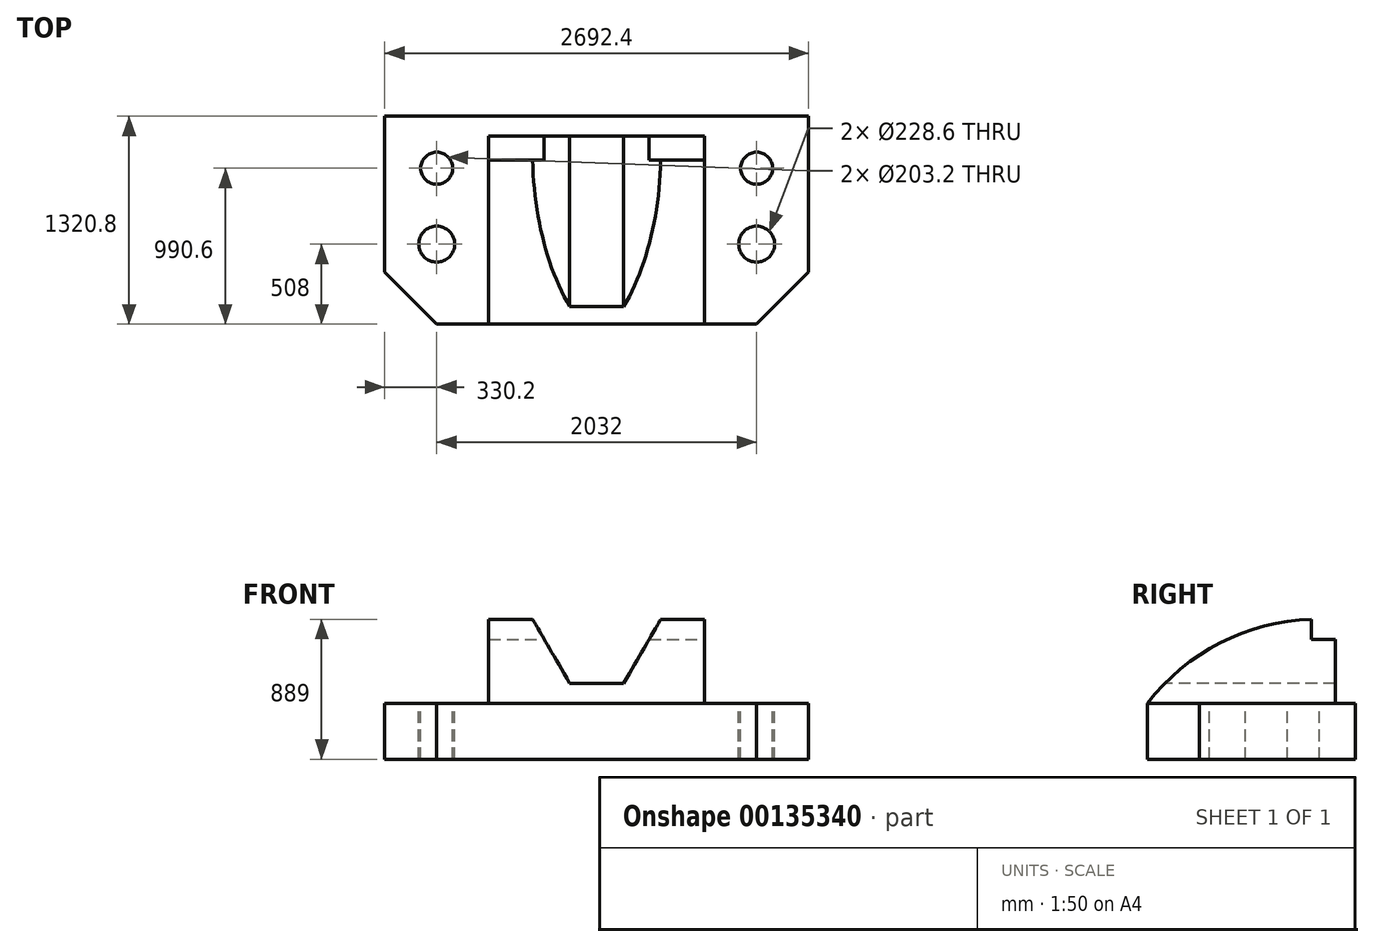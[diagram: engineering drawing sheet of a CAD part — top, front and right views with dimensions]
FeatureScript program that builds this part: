
annotation { "Feature Type Name" : "Feature", "Feature Type Description" : "" }
export const myFeature = defineFeature(function(context is Context, id is Id, definition is map)
    precondition{}
    {
        {
            var Q0;
            Q0=qCreatedBy(makeId("Top.planeOp"),FACE);
            var sketch = newSketch(context, id + "F0", { "sketchPlane" : qUnion([Q0])});
            skLineSegment(sketch, "E0.bottom", {"start": v(1346.2, -660.4) * mm, "end": v(-1346.2, -660.4) * mm});
            skLineSegment(sketch, "E0.top", {"start": v(1346.2, 660.4) * mm, "end": v(-1346.2, 660.4) * mm});
            skLineSegment(sketch, "E0.left", {"start": v(1346.2, -660.4) * mm, "end": v(1346.2, 660.4) * mm});
            skLineSegment(sketch, "E0.right", {"start": v(-1346.2, -660.4) * mm, "end": v(-1346.2, 660.4) * mm});
            skPoint(sketch, "E0.middle", {"position": v(0, 0) * mm});
            skSolve(sketch);
        }
        {
            var Q0;
            Q0 = qSketchRegion(id + "F0", true);
            var Q1;
            Q1=makeQuery(id+"F0.imprint","IMPRINT",FACE,{"disambiguationData":[TD([[makeQuery(id+"F0.imprint","IMPRINT",EDGE,{"derivedFrom":sQuery(id+"F0.wireOp",EDGE,"E0.bottom")}),-1.0]])]});
            extrude(context, id + "F1", {"entities" : qUnion([Q0, Q1]), "oppositeDirection" : true, "depth" : 355.6 * mm});
        }
        {
            var Q0;
            Q0=makeQuery(id+"F1.opExtrude","CAP_FACE",FACE,{"disambiguationData":[OSD([sQuery(id+"F0.wireOp",EDGE,"E0.bottom"),sQuery(id+"F0.wireOp",EDGE,"E0.top"),sQuery(id+"F0.wireOp",EDGE,"E0.left"),sQuery(id+"F0.wireOp",EDGE,"E0.right")])],"isStart":true});
            var sketch = newSketch(context, id + "F2", { "sketchPlane" : qUnion([Q0])});
            skLineSegment(sketch, "E1", {"start": v(1346.2, -660.4) * mm, "end": v(1346.2, -330.2) * mm});
            skLineSegment(sketch, "E2", {"start": v(1346.2, -660.4) * mm, "end": v(1016, -660.4) * mm});
            skLineSegment(sketch, "E3", {"start": v(1016, -660.4) * mm, "end": v(1346.2, -330.2) * mm});
            skLineSegment(sketch, "E4.MirrorCS", {"start": v(-1346.2, -660.4) * mm, "end": v(-1346.2, -330.2) * mm});
            skLineSegment(sketch, "E5.MirrorCS", {"start": v(-1346.2, -660.4) * mm, "end": v(-1016, -660.4) * mm});
            skLineSegment(sketch, "E6.MirrorCS", {"start": v(-1016, -660.4) * mm, "end": v(-1346.2, -330.2) * mm});
            skCircle(sketch, "E7", {"center": v(1016, -152.4) * mm, "radius": 114.3 * mm});
            skCircle(sketch, "E8", {"center": v(1016, 330.2) * mm, "radius": 101.6 * mm});
            skCircle(sketch, "E9.MirrorC", {"center": v(-1016, 330.2) * mm, "radius": 101.6 * mm});
            skCircle(sketch, "E10.MirrorC", {"center": v(-1016, -152.4) * mm, "radius": 114.3 * mm});
            skSolve(sketch);
        }
        {
            var Q0;
            Q0 = qSketchRegion(id + "F2", true);
            extrude(context, id + "F3", {"entities" : qUnion([Q0]), "operationType" : NewBodyOperationType.REMOVE, "endBound" : BoundingType.THROUGH_ALL, "oppositeDirection" : true, "depth" : 25.4 * mm});
        }
        {
            var Q0;
            Q0=makeQuery(id+"F1.opExtrude","SWEPT_FACE",FACE,{"disambiguationData":[OSD([sQuery(id+"F0.wireOp",EDGE,"E0.bottom")])]});
            var sketch = newSketch(context, id + "F4", { "sketchPlane" : qUnion([Q0])});
            skLineSegment(sketch, "E11", {"start": v(0, 0) * mm, "end": v(685.8, 0) * mm});
            skLineSegment(sketch, "E12", {"start": v(685.8, 0) * mm, "end": v(685.8, 533.4) * mm});
            skLineSegment(sketch, "E13", {"start": v(685.8, 533.4) * mm, "end": v(0, 533.4) * mm});
            skLineSegment(sketch, "E14.MirrorCS", {"start": v(-685.8, 533.4) * mm, "end": v(0, 533.4) * mm});
            skLineSegment(sketch, "E15.MirrorCS", {"start": v(-685.8, 0) * mm, "end": v(-685.8, 533.4) * mm});
            skLineSegment(sketch, "E16.MirrorCS", {"start": v(0, 0) * mm, "end": v(-685.8, 0) * mm});
            skSolve(sketch);
        }
        {
            var Q0;
            Q0=makeQuery(id+"F4.imprint","IMPRINT",FACE,{"disambiguationData":[TD([[makeQuery(id+"F4.imprint","IMPRINT",EDGE,{"derivedFrom":sQuery(id+"F4.wireOp",EDGE,"E11")}),-1.0]])]});
            var Q1;
            Q1=makeQuery(id+"F1.opExtrude","SWEPT_FACE",FACE,{"disambiguationData":[OSD([sQuery(id+"F0.wireOp",EDGE,"E0.top")])]});
            extrude(context, id + "F5", {"entities" : qUnion([Q0]), "operationType" : NewBodyOperationType.ADD, "endBound" : BoundingType.UP_TO_SURFACE, "oppositeDirection" : true, "endBoundEntityFace" : qUnion([Q1]), "depth" : 203.6 * mm});
        }
        {
            var Q0;
            Q0=makeQuery(id+"F5.opExtrude","SWEPT_FACE",FACE,{"disambiguationData":[OSD([sQuery(id+"F4.wireOp",EDGE,"E12")])]});
            var sketch = newSketch(context, id + "F6", { "sketchPlane" : qUnion([Q0])});
            skPoint(sketch, "E17.second.point", {"position": v(-660.4, 0) * mm});
            skArc(sketch, "E18", {"start": v(381, 533.4) * mm, "mid": v(-199.43, 383.32) * mm, "end": v(-660.4, 0) * mm});
            skLineSegment(sketch, "E19", {"start": v(-660.4, 0) * mm, "end": v(-660.4, 533.4) * mm});
            skLineSegment(sketch, "E20", {"start": v(-660.4, 533.4) * mm, "end": v(381, 533.4) * mm});
            skLineSegment(sketch, "E21", {"start": v(381, 533.4) * mm, "end": v(660.4, 533.4) * mm});
            skLineSegment(sketch, "E22", {"start": v(381, 533.4) * mm, "end": v(381, 406.4) * mm});
            skLineSegment(sketch, "E23", {"start": v(381, 406.4) * mm, "end": v(533.4, 406.4) * mm});
            skLineSegment(sketch, "E24", {"start": v(660.4, 406.4) * mm, "end": v(660.4, 533.4) * mm});
            skLineSegment(sketch, "E25", {"start": v(660.4, 406.4) * mm, "end": v(660.4, 0) * mm});
            skLineSegment(sketch, "E26", {"start": v(660.4, 0) * mm, "end": v(533.4, 0) * mm});
            skLineSegment(sketch, "E27", {"start": v(533.4, 0) * mm, "end": v(533.4, 406.4) * mm});
            skSolve(sketch);
        }
        {
            var Q0;
            Q0 = qSketchRegion(id + "F6", true);
            extrude(context, id + "F7", {"entities" : qUnion([Q0]), "operationType" : NewBodyOperationType.REMOVE, "endBound" : BoundingType.THROUGH_ALL, "oppositeDirection" : true, "depth" : 25.4 * mm});
        }
        {
            var Q0;
            Q0=makeQuery(id+"F5.boolean.opBoolean","MERGE",FACE,{"derivedFrom":[makeQuery(id+"F1.opExtrude","SWEPT_FACE",FACE,{"disambiguationData":[OSD([sQuery(id+"F0.wireOp",EDGE,"E0.bottom")])]}),makeQuery(id+"F5.opExtrude","CAP_FACE",FACE,{"disambiguationData":[OSD([sQuery(id+"F4.wireOp",EDGE,"E11"),sQuery(id+"F4.wireOp",EDGE,"E12"),sQuery(id+"F4.wireOp",EDGE,"E13"),sQuery(id+"F4.wireOp",EDGE,"E14.MirrorCS"),sQuery(id+"F4.wireOp",EDGE,"E15.MirrorCS"),sQuery(id+"F4.wireOp",EDGE,"E16.MirrorCS")])],"isStart":true})]});
            var sketch = newSketch(context, id + "F8", { "sketchPlane" : qUnion([Q0])});
            skLineSegment(sketch, "E28", {"start": v(0, 0) * mm, "end": v(0, 533.4) * mm, "construction": true});
            skCircle(sketch, "E29", {"center": v(0, 533.4) * mm, "radius": 406.4 * mm, "construction": true});
            skLineSegment(sketch, "E30", {"start": v(0, 127) * mm, "end": v(-685.8, 127) * mm, "construction": true});
            skLineSegment(sketch, "E31.MirrorCS", {"start": v(0, 127) * mm, "end": v(685.8, 127) * mm, "construction": true});
            skLineSegment(sketch, "E32", {"start": v(406.4, 533.4) * mm, "end": v(171.76, 127) * mm});
            skLineSegment(sketch, "E33.MirrorCS", {"start": v(-406.4, 533.4) * mm, "end": v(-171.76, 127) * mm});
            skLineSegment(sketch, "E34", {"start": v(-406.4, 533.4) * mm, "end": v(406.4, 533.4) * mm});
            skLineSegment(sketch, "E35", {"start": v(-171.76, 127) * mm, "end": v(171.76, 127) * mm});
            skSolve(sketch);
        }
        {
            var Q0;
            Q0 = qSketchRegion(id + "F8", true);
            extrude(context, id + "F9", {"entities" : qUnion([Q0]), "operationType" : NewBodyOperationType.REMOVE, "endBound" : BoundingType.THROUGH_ALL, "oppositeDirection" : true, "depth" : 25.4 * mm});
        }
    });
